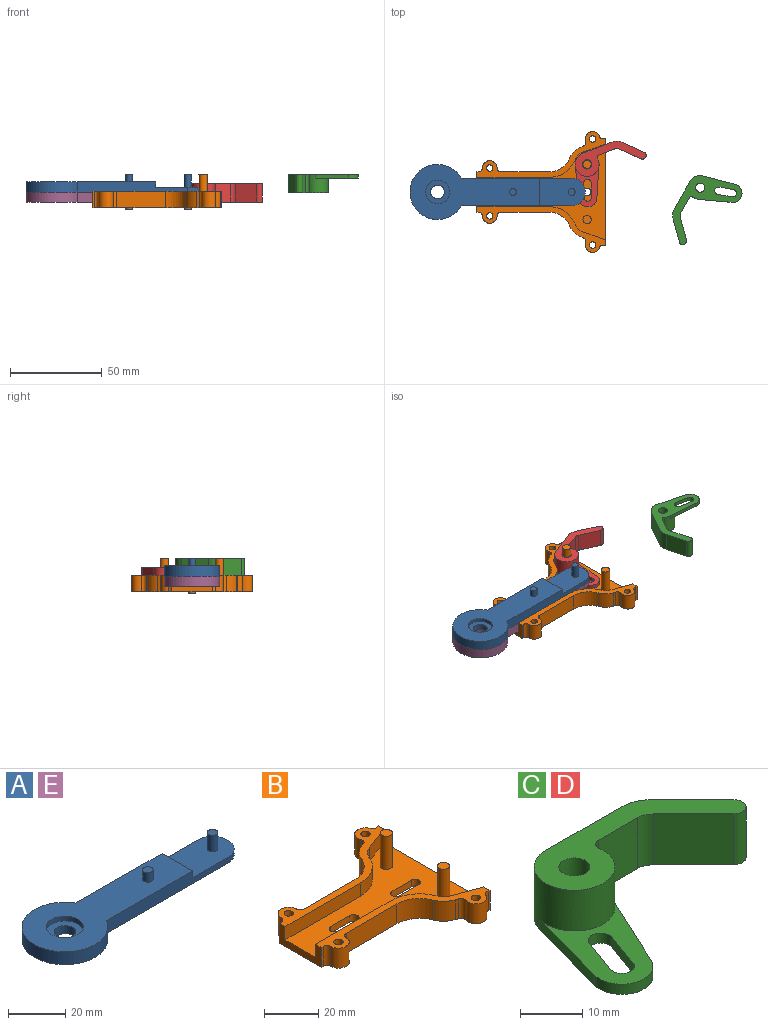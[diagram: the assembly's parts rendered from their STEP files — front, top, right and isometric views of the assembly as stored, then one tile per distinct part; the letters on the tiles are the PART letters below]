
ASSEMBLY  parts=5 mates=7
PART A: 15 faces, bbox 95.5x30x9.5 mm
  f0: plane 60.01x5.5mm, normal (0,-1,0), area 277.6mm2, adj f2,f3,f4,f5,f6,f7
  f1: plane 60.01x5.5mm, normal (0,1,0), area 277.6mm2, adj f2,f3,f4,f5,f6,f7
  f2: cylinder r=7.5mm len=15mm, axis (0,0,-1), area 58.9mm2, adj f0,f1,f5,f7
  f3: cylinder r=15mm len=30mm, axis (0,0,-1), area 432mm2, adj f0,f1,f4,f5
  f4: plane 70.5x30mm, normal (0,0,1), area 1180.6mm2, adj f0,f1,f3,f6,f8,f14
  f5: plane 95.5x30mm, normal (0,0,-1), area 1630.8mm2, adj f0,f1,f2,f3,f12
  f6: plane 15x3mm, normal (1,0,0), area 45mm2, adj f0,f1,f4,f7
  f7: plane 25x15mm, normal (0,0,1), area 340.1mm2, adj f0,f1,f2,f6,f10
  f8: cylinder r=1.85mm len=4mm, axis (0,0,-1), area 46.5mm2, adj f4,f9
  f9: plane 3.7x3.7mm, normal (0,0,1), area 10.8mm2, adj f8
  f10: cylinder r=1.85mm len=7mm, axis (0,0,-1), area 81.4mm2, adj f7,f11
  f11: plane 3.7x3.7mm, normal (0,0,1), area 10.8mm2, adj f10
  f12: cylinder r=3.75mm len=7.5mm, axis (0,0,1), area 82.5mm2, adj f5,f13
  f13: plane 13x13mm, normal (0,0,1), area 88.6mm2, adj f12,f14
  f14: cylinder r=6.5mm len=13mm, axis (0,0,1), area 81.7mm2, adj f4,f13
PART B: 62 faces, bbox 70x65.7x18 mm
  f0: plane 58.56x9mm, normal (1,0,0), area 214mm2, adj f2,f5,f11,f16,f20,f29,f32,f42
  f1: plane 22x9mm, normal (-1,0,0), area 102mm2, adj f2,f4,f11,f19,f20,f29,f31,f45
  f2: plane 70x24.87mm, normal (0,0,1), area 296.4mm2, adj f0,f1,f3,f4,f5,f6,f7,f8
  f3: cylinder r=4mm len=9mm, axis (0,0,-1), area 113.1mm2, adj f2,f11,f12,f13
  f4: plane 9x1mm, normal (0,1,0), area 9mm2, adj f1,f2,f11,f12
  f5: plane 9x0.67mm, normal (-0.34,0.94,0), area 6.4mm2, adj f0,f2,f11,f14
  f6: cylinder r=4mm len=9mm, axis (0,0,-1), area 113.1mm2, adj f2,f11,f14,f15
  f7: plane 9x1.48mm, normal (-0.34,0.94,0), area 14.2mm2, adj f2,f8,f11,f15
  f8: cylinder r=10mm len=9mm, axis (0,0,-1), area 76.5mm2, adj f2,f7,f9,f11
  f9: cylinder r=12mm len=11.18mm, axis (0,0,-1), area 129.5mm2, adj f2,f8,f10,f11
  f10: plane 26.51x9mm, normal (0,1,0), area 238.6mm2, adj f2,f9,f11,f13
  f11: plane 70x65.73mm, normal (0,0,-1), area 2117.1mm2, adj f0,f1,f3,f4,f5,f6,f7,f8
  f12: cylinder r=2mm len=9mm, axis (0,0,-1), area 28.3mm2, adj f2,f3,f4,f11
  f13: cylinder r=2mm len=9mm, axis (0,0,-1), area 28.3mm2, adj f2,f3,f10,f11
  f14: cylinder r=2mm len=9mm, axis (0,0,-1), area 28.3mm2, adj f2,f5,f6,f11
  f15: cylinder r=2mm len=9mm, axis (0,0,-1), area 28.3mm2, adj f2,f6,f7,f11
  f16: plane 12.39x6mm, normal (0.34,-0.94,0), area 79.1mm2, adj f0,f2,f17,f20
  f17: cylinder r=7mm len=6mm, axis (0,0,1), area 35.7mm2, adj f2,f16,f18,f20
  f18: cylinder r=15mm len=13.97mm, axis (0,0,1), area 107.9mm2, adj f2,f17,f19,f20
  f19: plane 39.51x6mm, normal (0,-1,0), area 237mm2, adj f1,f2,f18,f20
  f20: plane 70x52.18mm, normal (0,0,1), area 1549.1mm2, adj f0,f1,f16,f17,f18,f19,f27,f42
  f21: cylinder r=1.75mm len=7mm, axis (0,0,-1), area 77mm2, adj f2,f22
  f22: plane 5.5x5.5mm, normal (0,0,-1), area 14.1mm2, adj f21,f23
  f23: cylinder r=2.75mm len=5.5mm, axis (0,0,-1), area 34.6mm2, adj f11,f22
  f24: cylinder r=1.75mm len=7mm, axis (0,0,-1), area 77mm2, adj f2,f25
  f25: plane 5.5x5.5mm, normal (0,0,-1), area 14.1mm2, adj f24,f26
  f26: cylinder r=2.75mm len=5.5mm, axis (0,0,-1), area 34.6mm2, adj f11,f25
  f27: cylinder r=2.25mm len=15mm, axis (0,0,-1), area 212.1mm2, adj f20,f28
  f28: plane 4.5x4.5mm, normal (0,0,1), area 15.9mm2, adj f27
  f29: plane 70x24.87mm, normal (0,0,1), area 296.4mm2, adj f0,f1,f30,f31,f32,f33,f34,f35
  f30: cylinder r=4mm len=9mm, axis (0,0,-1), area 113.1mm2, adj f11,f29,f38,f39
  f31: plane 9x1mm, normal (0,-1,0), area 9mm2, adj f1,f11,f29,f38
  f32: plane 9x0.67mm, normal (-0.34,-0.94,0), area 6.4mm2, adj f0,f11,f29,f40
  f33: cylinder r=4mm len=9mm, axis (0,0,-1), area 113.1mm2, adj f11,f29,f40,f41
  f34: plane 9x1.48mm, normal (-0.34,-0.94,0), area 14.2mm2, adj f11,f29,f35,f41
  f35: cylinder r=10mm len=9mm, axis (0,0,-1), area 76.5mm2, adj f11,f29,f34,f36
  f36: cylinder r=12mm len=11.18mm, axis (0,0,-1), area 129.5mm2, adj f11,f29,f35,f37
  f37: plane 26.51x9mm, normal (0,-1,0), area 238.6mm2, adj f11,f29,f36,f39
  f38: cylinder r=2mm len=9mm, axis (0,0,-1), area 28.3mm2, adj f11,f29,f30,f31
  f39: cylinder r=2mm len=9mm, axis (0,0,-1), area 28.3mm2, adj f11,f29,f30,f37
  f40: cylinder r=2mm len=9mm, axis (0,0,-1), area 28.3mm2, adj f11,f29,f32,f33
  f41: cylinder r=2mm len=9mm, axis (0,0,-1), area 28.3mm2, adj f11,f29,f33,f34
  f42: plane 12.39x6mm, normal (0.34,0.94,0), area 79.1mm2, adj f0,f20,f29,f43
  f43: cylinder r=7mm len=6mm, axis (0,0,1), area 35.7mm2, adj f20,f29,f42,f44
  f44: cylinder r=15mm len=13.97mm, axis (0,0,1), area 107.9mm2, adj f20,f29,f43,f45
  f45: plane 39.51x6mm, normal (0,1,0), area 237mm2, adj f1,f20,f29,f44
  f46: cylinder r=1.75mm len=7mm, axis (0,0,-1), area 77mm2, adj f29,f47
  f47: plane 5.5x5.5mm, normal (0,0,-1), area 14.1mm2, adj f46,f48
  f48: cylinder r=2.75mm len=5.5mm, axis (0,0,-1), area 34.6mm2, adj f11,f47
  f49: cylinder r=1.75mm len=7mm, axis (0,0,-1), area 77mm2, adj f29,f50
  f50: plane 5.5x5.5mm, normal (0,0,-1), area 14.1mm2, adj f49,f51
  f51: cylinder r=2.75mm len=5.5mm, axis (0,0,-1), area 34.6mm2, adj f11,f50
  f52: cylinder r=2.25mm len=15mm, axis (0,0,-1), area 212.1mm2, adj f20,f53
  f53: plane 4.5x4.5mm, normal (0,0,1), area 15.9mm2, adj f52
  f54: cylinder r=2mm len=4mm, axis (0,0,1), area 18.8mm2, adj f11,f20,f55,f57
  f55: plane 10x3mm, normal (0,1,0), area 30mm2, adj f11,f20,f54,f56
  f56: cylinder r=2mm len=4mm, axis (0,0,1), area 18.8mm2, adj f11,f20,f55,f57
  f57: plane 10x3mm, normal (0,-1,0), area 30mm2, adj f11,f20,f54,f56
  f58: cylinder r=2mm len=4mm, axis (0,0,1), area 18.8mm2, adj f11,f20,f59,f61
  f59: plane 10x3mm, normal (0,-1,0), area 30mm2, adj f11,f20,f58,f60
  f60: cylinder r=2mm len=4mm, axis (0,0,1), area 18.8mm2, adj f11,f20,f59,f61
  f61: plane 10x3mm, normal (0,1,0), area 30mm2, adj f11,f20,f58,f60
PART C: 20 faces, bbox 43.1x28.4x10 mm
  f0: plane 23.62x17.06mm, normal (0,0,1), area 136.1mm2, adj f2,f3,f4,f5,f16,f17,f18,f19
  f1: plane 43.06x28.41mm, normal (0,0,-1), area 375.3mm2, adj f2,f3,f4,f5,f6,f7,f8,f9
  f2: plane 17.31x4.71mm, normal (-0.96,0.26,0), area 35.9mm2, adj f0,f1,f3,f5
  f3: cylinder r=5mm len=9.54mm, axis (0,0,-1), area 29.7mm2, adj f0,f1,f2,f4
  f4: plane 16.29x7.52mm, normal (0.91,-0.42,0), area 35.9mm2, adj f0,f1,f3,f5
  f5: cylinder r=6.5mm len=13mm, axis (0,0,-1), area 275.8mm2, adj f0,f1,f2,f4,f10,f11,f12
  f6: plane 10x8.96mm, normal (0,-1,0), area 89.6mm2, adj f1,f11,f12,f13
  f7: plane 10x9.12mm, normal (-0.71,-0.71,0), area 128.9mm2, adj f1,f8,f11,f13
  f8: cylinder r=2mm len=10mm, axis (0,0,-1), area 62.8mm2, adj f1,f7,f9,f11
  f9: plane 10x9.12mm, normal (0.71,0.71,0), area 128.9mm2, adj f1,f8,f11,f14
  f10: plane 16.89x10mm, normal (0,1,0), area 168.9mm2, adj f1,f5,f11,f14
  f11: plane 38.4x14.73mm, normal (0,0,1), area 239.2mm2, adj f5,f6,f7,f8,f9,f10,f12,f13
  f12: cylinder r=1.5mm len=10mm, axis (0,0,-1), area 25.4mm2, adj f1,f5,f6,f11
  f13: cylinder r=3.5mm len=10mm, axis (0,0,1), area 27.5mm2, adj f1,f6,f7,f11
  f14: cylinder r=7.5mm len=10mm, axis (0,0,-1), area 58.9mm2, adj f1,f9,f10,f11
  f15: cylinder r=2.5mm len=10mm, axis (0,0,1), area 157.1mm2, adj f1,f11
  f16: plane 7.52x2.74mm, normal (-0.94,0.34,0), area 16mm2, adj f0,f1,f17,f19
  f17: cylinder r=2mm len=3.88mm, axis (0,0,1), area 12.6mm2, adj f0,f1,f16,f18
  f18: plane 7.52x2.74mm, normal (0.94,-0.34,0), area 16mm2, adj f0,f1,f17,f19
  f19: cylinder r=2mm len=3.88mm, axis (0,0,1), area 12.6mm2, adj f0,f1,f16,f18
PART D: same geometry as C
PART E: same geometry as A
PLACE A t=(-29,-6.68,12.76)mm
PLACE B t=(-7.61,-6.68,4.26)mm fixed
PLACE C rot(axis=(0.5,-0.86,0),180deg) t=(113.98,-4.31,22.26)mm
PLACE D rot(axis=(0,0,1),21deg) t=(52.39,8.32,7.26)mm
PLACE E rot(axis=(1,0,0),180deg) t=(-29,-6.68,12.76)mm
MATE pin_slot E.f8 <-> B.f20  axis (0,0,-1) through (12,-6.68,7.26)mm
MATE cylindrical D.f5 <-> B.f8  axis (0,0,1) through (52.39,8.32,17.26)mm
MATE parallel A.f0 <-> E.f1  axis (0,-1,0) through (9.97,-14.18,15.27)mm
MATE parallel E.f1 <-> B.f37  axis (0,-1,0) through (9.97,-14.18,10.24)mm
MATE planar D.f1 <-> B.f20  axis (0,0,-1) through (58.18,6.3,7.26)mm
MATE cylindrical A.f3 <-> E.f3  axis (0,0,1) through (-29,-6.68,16.26)mm
MATE planar E.f5 <-> A.f5  axis (0,0,1) through (-1.31,-6.68,12.76)mm
